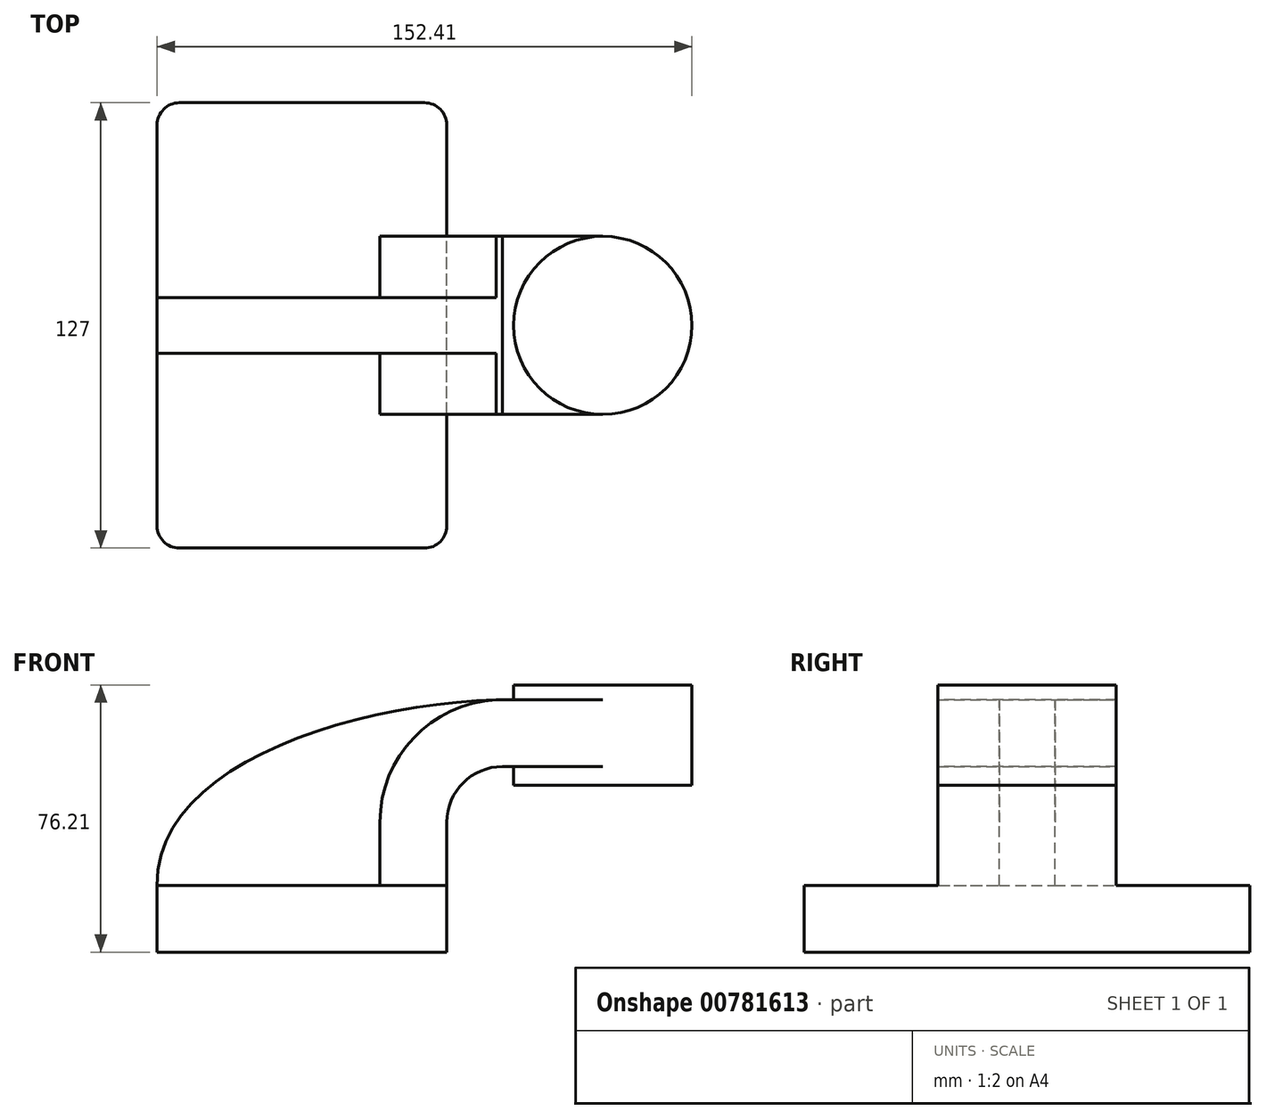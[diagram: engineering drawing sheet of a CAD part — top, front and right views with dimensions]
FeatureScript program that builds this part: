
annotation { "Feature Type Name" : "Feature", "Feature Type Description" : "" }
export const myFeature = defineFeature(function(context is Context, id is Id, definition is map)
    precondition{}
    {
        {
            var Q0;
            Q0=qCreatedBy(makeId("Front.planeOp"),FACE);
            var sketch = newSketch(context, id + "F0", { "sketchPlane" : qUnion([Q0])});
            skLineSegment(sketch, "E0.bottom", {"start": v(-41.28, -9.53) * mm, "end": v(41.28, -9.53) * mm});
            skLineSegment(sketch, "E0.top", {"start": v(-41.28, 9.52) * mm, "end": v(41.28, 9.52) * mm});
            skLineSegment(sketch, "E0.left", {"start": v(-41.28, -9.53) * mm, "end": v(-41.28, 9.53) * mm});
            skLineSegment(sketch, "E0.right", {"start": v(41.28, -9.53) * mm, "end": v(41.28, 9.52) * mm});
            skPoint(sketch, "E0.middle", {"position": v(0, 0) * mm});
            skLineSegment(sketch, "E1.bottom", {"start": v(60.32, 38.1) * mm, "end": v(111.12, 38.1) * mm});
            skLineSegment(sketch, "E1.top", {"start": v(60.32, 66.67) * mm, "end": v(111.12, 66.67) * mm});
            skLineSegment(sketch, "E1.left", {"start": v(60.32, 38.1) * mm, "end": v(60.32, 66.67) * mm});
            skLineSegment(sketch, "E1.right", {"start": v(111.12, 38.1) * mm, "end": v(111.12, 66.67) * mm});
            skPoint(sketch, "E1.middle", {"position": v(85.72, 52.39) * mm});
            skLineSegment(sketch, "E2", {"start": v(41.27, 9.52) * mm, "end": v(41.27, 27.5) * mm});
            skArc(sketch, "E3", {"start": v(41.27, 27.5) * mm, "mid": v(45.92, 38.73) * mm, "end": v(57.15, 43.38) * mm});
            skLineSegment(sketch, "E4", {"start": v(57.15, 43.38) * mm, "end": v(85.72, 43.38) * mm});
            skLineSegment(sketch, "E5.0", {"start": v(57.15, 62.43) * mm, "end": v(85.72, 62.43) * mm});
            skArc(sketch, "E5.1", {"start": v(22.23, 27.5) * mm, "mid": v(32.45, 52.2) * mm, "end": v(57.15, 62.43) * mm});
            skLineSegment(sketch, "E5.2", {"start": v(22.23, 9.52) * mm, "end": v(22.23, 27.5) * mm});
            skFitSpline(sketch, "E6", {"points": [v(-41.28, 9.53) * mm, v(57.15, 62.43) * mm], "startDerivative": vector(-1.54, 103.95) * mm, "endDerivative": vector(126.55, 2.64) * mm});
            skLineSegment(sketch, "E7", {"start": v(85.72, 66.67) * mm, "end": v(85.72, 38.1) * mm});
            skSolve(sketch);
        }
        {
            var Q0;
            Q0=makeQuery(id+"F0.imprint","IMPRINT",FACE,{"disambiguationData":[TD([[makeQuery(id+"F0.imprint","IMPRINT",EDGE,{"derivedFrom":sQuery(id+"F0.wireOp",EDGE,"E0.bottom")}),1.0]])]});
            extrude(context, id + "F1", {"entities" : qUnion([Q0]), "endBound" : BoundingType.SYMMETRIC, "depth" : 127 * mm, "offsetDistance" : 25.4 * mm});
        }
        {
            var Q0;
            {var subQ0=sQuery(id+"F0.wireOp",EDGE,"E2");Q0=makeQuery(id+"F0.imprint","IMPRINT",FACE,{"disambiguationData":[TD([[makeQuery(id+"F0.imprint","IMPRINT",EDGE,{"derivedFrom":subQ0}),1.0]])]});}
            var Q1;
            {var subQ0=sQuery(id+"F0.wireOp",EDGE,"E4");var subQ1=sQuery(id+"F0.wireOp",EDGE,"E1.left");var subQ2=makeQuery(id+"F0.imprint","INTERSECT",VERTEX,{"derivedFrom":[subQ1,subQ0]});Q1=makeQuery(id+"F0.imprint","IMPRINT",FACE,{"disambiguationData":[TD([[makeQuery(id+"F0.imprint","IMPRINT",EDGE,{"disambiguationData":[TD([[subQ2,-1.0]])],"derivedFrom":subQ1}),-1.0]])]});}
            extrude(context, id + "F2", {"entities" : qUnion([Q0, Q1]), "operationType" : NewBodyOperationType.ADD, "endBound" : BoundingType.SYMMETRIC, "depth" : 50.8 * mm, "offsetDistance" : 25.4 * mm});
        }
        {
            var Q0;
            {var subQ3=sQuery(id+"F0.wireOp",EDGE,"E5.2");Q0=makeQuery(id+"F0.imprint","IMPRINT",FACE,{"disambiguationData":[TD([[makeQuery(id+"F0.imprint","IMPRINT",EDGE,{"derivedFrom":subQ3}),1.0]])]});}
            extrude(context, id + "F3", {"entities" : qUnion([Q0]), "operationType" : NewBodyOperationType.ADD, "endBound" : BoundingType.SYMMETRIC, "depth" : 15.88 * mm, "offsetDistance" : 25.4 * mm});
        }
        {
            var Q0;
            {var subQ4=sQuery(id+"F0.wireOp",EDGE,"E1.right");Q0=makeQuery(id+"F0.imprint","IMPRINT",FACE,{"disambiguationData":[TD([[makeQuery(id+"F0.imprint","IMPRINT",EDGE,{"derivedFrom":subQ4}),1.0]])]});}
            var Q1;
            Q1=sQuery(id+"F0.wireOp",EDGE,"E7");
            revolve(context, id + "F4", {"operationType" : NewBodyOperationType.ADD, "surfaceOperationType" : NewSurfaceOperationType.NEW, "entities" : qUnion([Q0]), "axis" : qUnion([Q1]), "revolveType" : RevolveType.FULL});
        }
        {
            var Q0;
            Q0=makeQuery(id+"F1.opExtrude","CAP_EDGE",EDGE,{"disambiguationData":[OSD([sQuery(id+"F0.wireOp",EDGE,"E0.right")])],"isStart":false});
            var Q1;
            Q1=makeQuery(id+"F1.opExtrude","CAP_EDGE",EDGE,{"disambiguationData":[OSD([sQuery(id+"F0.wireOp",EDGE,"E0.left")])],"isStart":false});
            var Q2;
            Q2=makeQuery(id+"F1.opExtrude","CAP_EDGE",EDGE,{"disambiguationData":[OSD([sQuery(id+"F0.wireOp",EDGE,"E0.right")])],"isStart":true});
            var Q3;
            Q3=makeQuery(id+"F1.opExtrude","CAP_EDGE",EDGE,{"disambiguationData":[OSD([sQuery(id+"F0.wireOp",EDGE,"E0.left")])],"isStart":true});
            fillet(context, id + "F5", {"entities" : qUnion([Q0, Q1, Q2, Q3]), "radius" : 6.35 * mm, "tangentPropagation" : true, "allowEdgeOverflow" : false});
        }
    });
